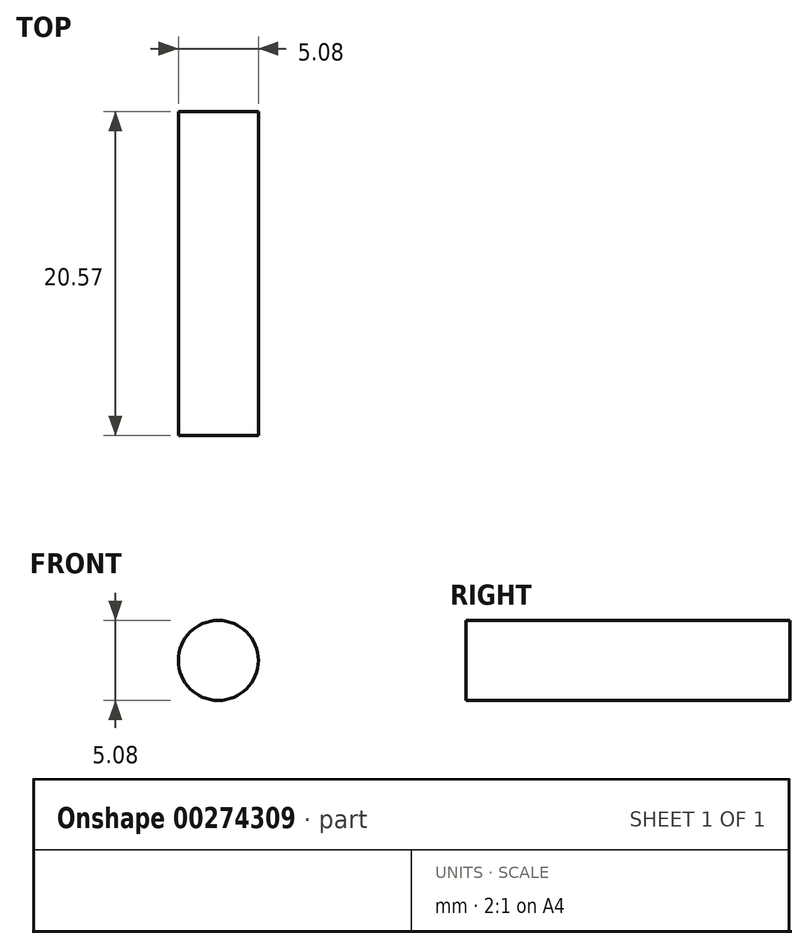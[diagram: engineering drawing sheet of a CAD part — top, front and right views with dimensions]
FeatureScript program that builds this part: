
annotation { "Feature Type Name" : "Feature", "Feature Type Description" : "" }
export const myFeature = defineFeature(function(context is Context, id is Id, definition is map)
    precondition{}
    {
        {
            var Q0;
            Q0=qCreatedBy(makeId("Front.planeOp"),FACE);
            var sketch = newSketch(context, id + "F0", { "sketchPlane" : qUnion([Q0])});
            skCircle(sketch, "E0", {"center": v(0, 0) * mm, "radius": 2.54 * mm});
            skSolve(sketch);
        }
        {
            var Q0;
            Q0=makeQuery(id+"F0.imprint","IMPRINT",FACE,{"disambiguationData":[TD([[makeQuery(id+"F0.imprint","IMPRINT",EDGE,{"derivedFrom":sQuery(id+"F0.wireOp",EDGE,"E0")}),1.0]])]});
            extrude(context, id + "F1", {"entities" : qUnion([Q0]), "depth" : 20.57 * mm});
        }
    });
